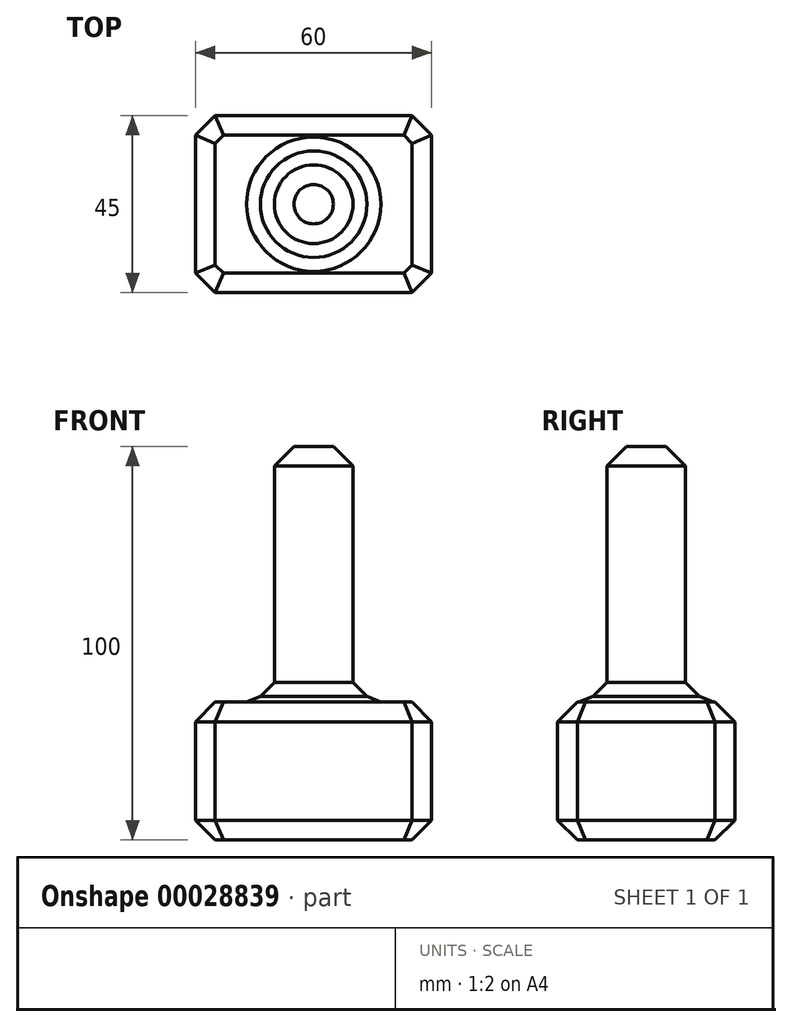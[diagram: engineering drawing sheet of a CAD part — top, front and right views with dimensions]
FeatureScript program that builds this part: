
annotation { "Feature Type Name" : "Feature", "Feature Type Description" : "" }
export const myFeature = defineFeature(function(context is Context, id is Id, definition is map)
    precondition{}
    {
        {
            var Q0;
            Q0=qCreatedBy(makeId("Top.planeOp"),FACE);
            var sketch = newSketch(context, id + "F0", { "sketchPlane" : qUnion([Q0])});
            skLineSegment(sketch, "E0.rect.bottom", {"start": v(30, 22.5) * mm, "end": v(-30, 22.5) * mm});
            skLineSegment(sketch, "E0.rect.top", {"start": v(30, -22.5) * mm, "end": v(-30, -22.5) * mm});
            skLineSegment(sketch, "E0.rect.left", {"start": v(30, 22.5) * mm, "end": v(30, -22.5) * mm});
            skLineSegment(sketch, "E0.rect.right", {"start": v(-30, 22.5) * mm, "end": v(-30, -22.5) * mm});
            skPoint(sketch, "E0.rect.middle", {"position": v(0, 0) * mm});
            skCircle(sketch, "E1", {"center": v(0, 0) * mm, "radius": 10 * mm});
            skSolve(sketch);
        }
        {
            var Q0;
            Q0=makeQuery(id+"F0.imprint","IMPRINT",FACE,{"disambiguationData":[TD([[makeQuery(id+"F0.imprint","IMPRINT",EDGE,{"derivedFrom":sQuery(id+"F0.wireOp",EDGE,"E0.rect.bottom")}),1.0]])]});
            var Q1;
            Q1=makeQuery(id+"F0.imprint","IMPRINT",FACE,{"disambiguationData":[TD([[makeQuery(id+"F0.imprint","IMPRINT",EDGE,{"derivedFrom":sQuery(id+"F0.wireOp",EDGE,"E1")}),1.0]])]});
            extrude(context, id + "F1", {"entities" : qUnion([Q0, Q1]), "depth" : 35 * mm});
        }
        {
            var Q0;
            Q0=makeQuery(id+"F0.imprint","IMPRINT",FACE,{"disambiguationData":[TD([[makeQuery(id+"F0.imprint","IMPRINT",EDGE,{"derivedFrom":sQuery(id+"F0.wireOp",EDGE,"E1")}),1.0]])]});
            extrude(context, id + "F2", {"entities" : qUnion([Q0]), "operationType" : NewBodyOperationType.ADD, "depth" : 100 * mm});
        }
        {
            var Q0;
            Q0=makeQuery(id+"F1.opExtrude","SWEPT_EDGE",EDGE,{"disambiguationData":[OSD([sQuery(id+"F0.wireOp",EDGE,"E0.rect.bottom"),sQuery(id+"F0.wireOp",EDGE,"E0.rect.right")])]});
            var Q1;
            Q1=makeQuery(id+"F1.opExtrude","SWEPT_EDGE",EDGE,{"disambiguationData":[OSD([sQuery(id+"F0.wireOp",EDGE,"E0.rect.top"),sQuery(id+"F0.wireOp",EDGE,"E0.rect.right")])]});
            var Q2;
            Q2=makeQuery(id+"F1.opExtrude","SWEPT_EDGE",EDGE,{"disambiguationData":[OSD([sQuery(id+"F0.wireOp",EDGE,"E0.rect.top"),sQuery(id+"F0.wireOp",EDGE,"E0.rect.left")])]});
            var Q3;
            Q3=makeQuery(id+"F1.opExtrude","SWEPT_EDGE",EDGE,{"disambiguationData":[OSD([sQuery(id+"F0.wireOp",EDGE,"E0.rect.bottom"),sQuery(id+"F0.wireOp",EDGE,"E0.rect.left")])]});
            chamfer(context, id + "F3", {"entities" : qUnion([Q0, Q1, Q2, Q3]), "width" : 5 * mm, "tangentPropagation" : true});
        }
        {
            var Q0;
            Q0=makeQuery(id+"F2.opExtrude","SWEPT_FACE",FACE,{"disambiguationData":[OSD([sQuery(id+"F0.wireOp",EDGE,"E1")])]});
            chamfer(context, id + "F4", {"entities" : qUnion([Q0]), "width" : 5 * mm, "tangentPropagation" : true});
        }
        {
            var Q0;
            Q0=makeQuery(id+"F1.opExtrude","CAP_FACE",FACE,{"disambiguationData":[OSD([sQuery(id+"F0.wireOp",EDGE,"E0.rect.bottom"),sQuery(id+"F0.wireOp",EDGE,"E0.rect.top"),sQuery(id+"F0.wireOp",EDGE,"E0.rect.left"),sQuery(id+"F0.wireOp",EDGE,"E0.rect.right")])],"isStart":false});
            var Q1;
            Q1=makeQuery(id+"F1.opExtrude","CAP_FACE",FACE,{"disambiguationData":[OSD([sQuery(id+"F0.wireOp",EDGE,"E0.rect.bottom"),sQuery(id+"F0.wireOp",EDGE,"E0.rect.top"),sQuery(id+"F0.wireOp",EDGE,"E0.rect.left"),sQuery(id+"F0.wireOp",EDGE,"E0.rect.right")])],"isStart":true});
            chamfer(context, id + "F5", {"entities" : qUnion([Q0, Q1]), "width" : 5 * mm, "tangentPropagation" : true});
        }
    });
